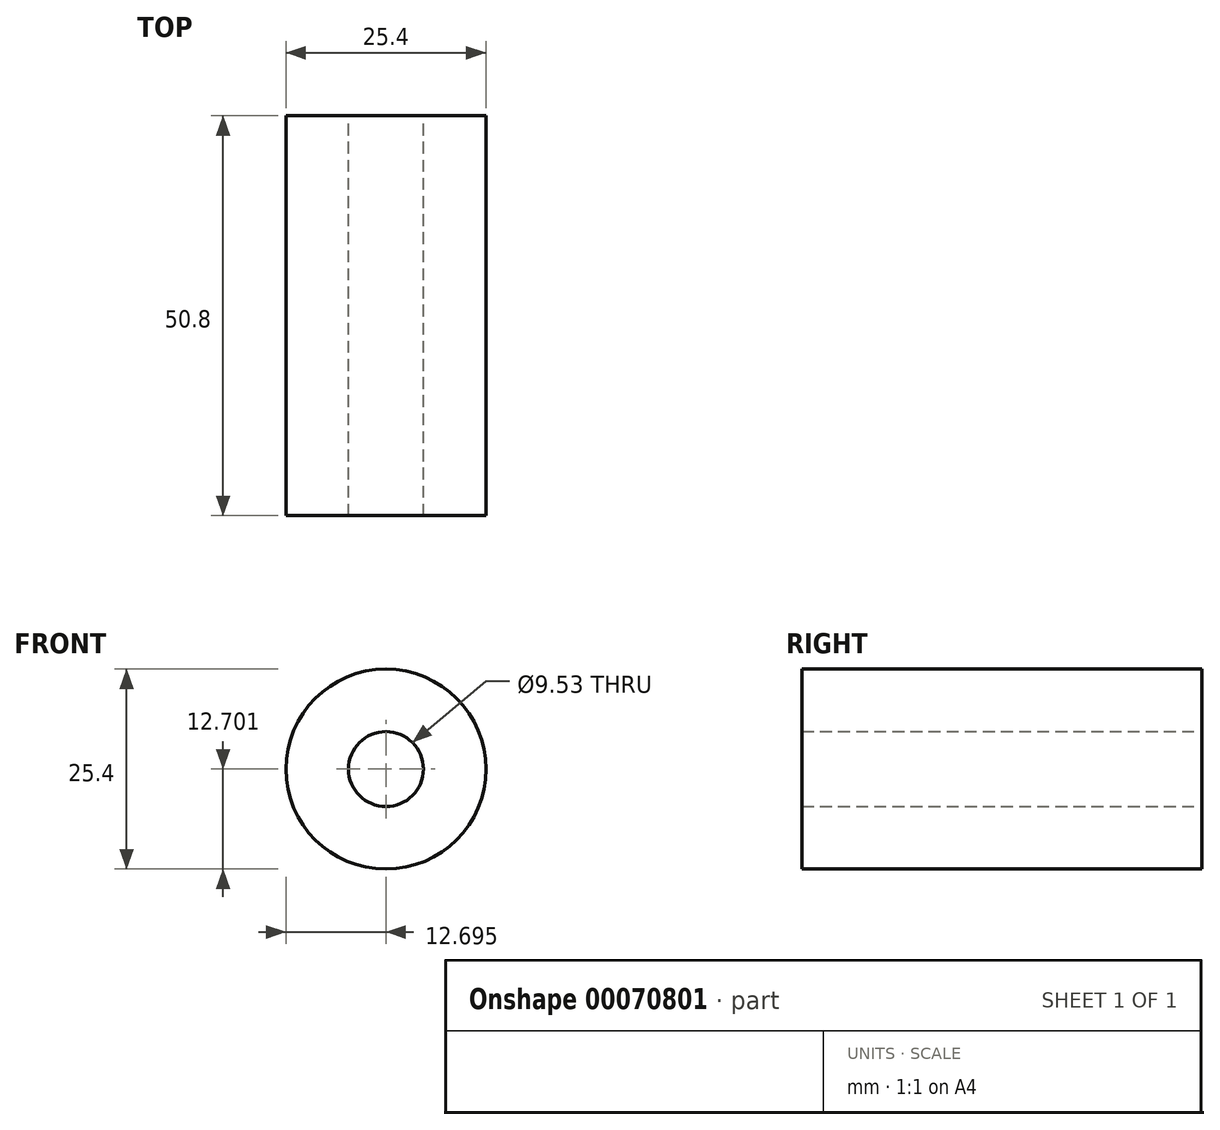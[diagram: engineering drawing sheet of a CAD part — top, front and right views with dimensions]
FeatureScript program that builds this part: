
annotation { "Feature Type Name" : "Feature", "Feature Type Description" : "" }
export const myFeature = defineFeature(function(context is Context, id is Id, definition is map)
    precondition{}
    {
        {
            var Q0;
            Q0=qCreatedBy(makeId("Front.planeOp"),FACE);
            var sketch = newSketch(context, id + "F0", { "sketchPlane" : qUnion([Q0])});
            skCircle(sketch, "E0", {"center": v(-6.7, 7.1) * mm, "radius": 12.7 * mm});
            skCircle(sketch, "E1", {"center": v(-6.7, 7.1) * mm, "radius": 4.76 * mm});
            skCircle(sketch, "E2", {"center": v(-6.7, 7.1) * mm, "radius": 2.39 * mm});
            skSolve(sketch);
        }
        {
            var Q0;
            Q0=makeQuery(id+"F0.imprint","IMPRINT",FACE,{"disambiguationData":[TD([[makeQuery(id+"F0.imprint","IMPRINT",EDGE,{"derivedFrom":sQuery(id+"F0.wireOp",EDGE,"E0")}),1.0]])]});
            extrude(context, id + "F1", {"entities" : qUnion([Q0]), "depth" : 25.4 * mm});
        }
        {
            var Q0;
            Q0=makeQuery(id+"F1.opExtrude","CAP_FACE",FACE,{"disambiguationData":[OSD([sQuery(id+"F0.wireOp",EDGE,"E0"),sQuery(id+"F0.wireOp",EDGE,"E1")])],"isStart":false});
            extrude(context, id + "F2", {"entities" : qUnion([Q0]), "operationType" : NewBodyOperationType.ADD, "depth" : 25.4 * mm});
        }
    });
